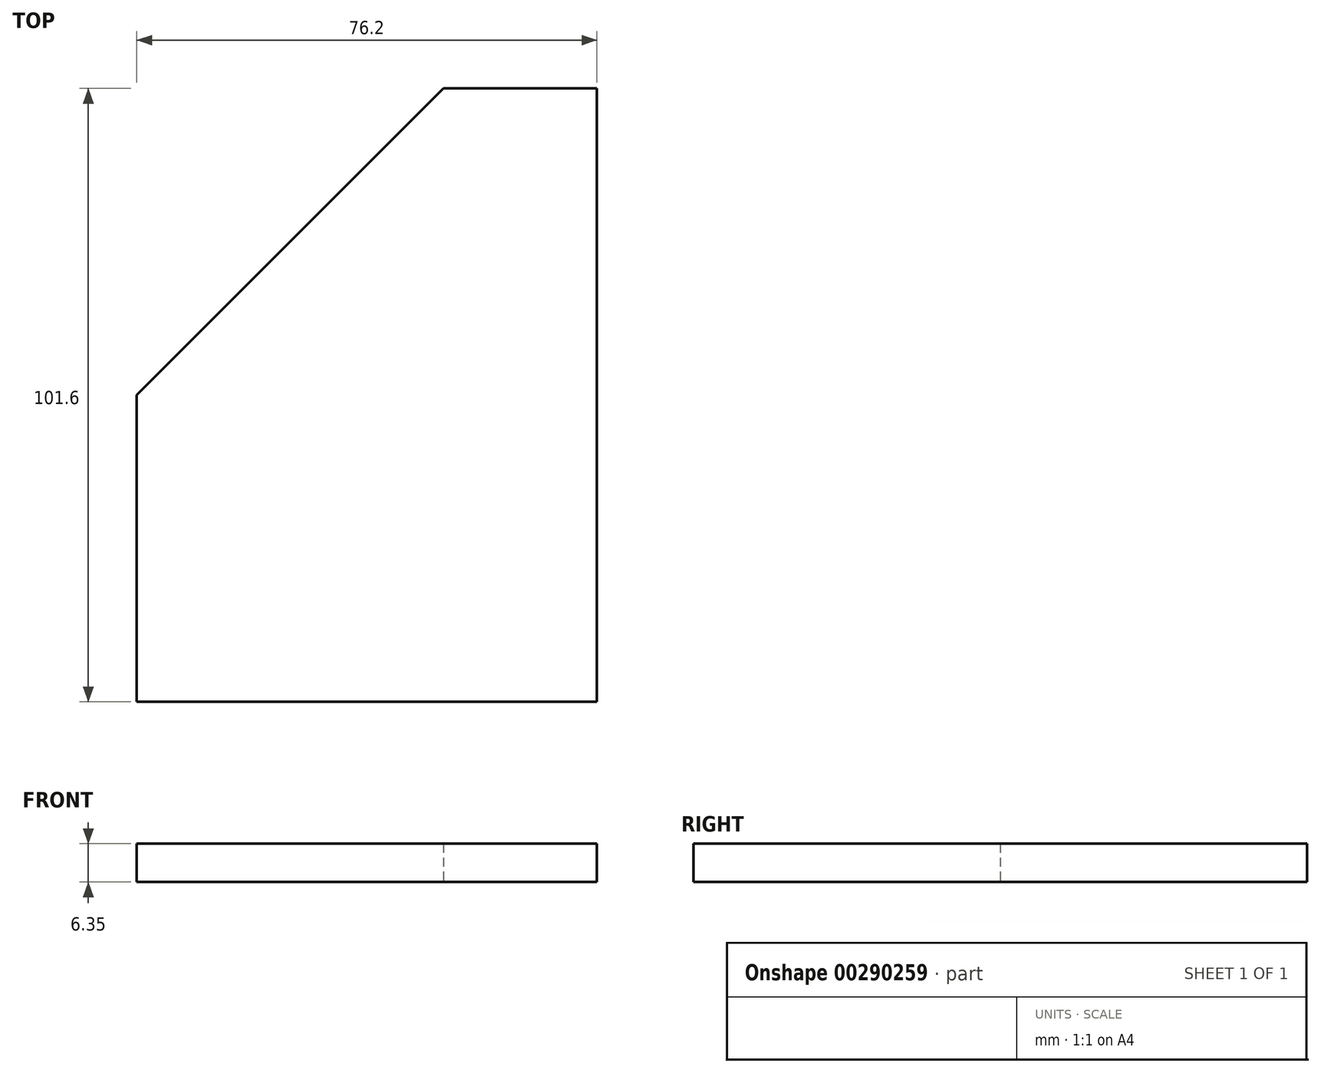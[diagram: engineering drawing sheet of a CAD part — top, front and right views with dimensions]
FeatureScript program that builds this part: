
annotation { "Feature Type Name" : "Feature", "Feature Type Description" : "" }
export const myFeature = defineFeature(function(context is Context, id is Id, definition is map)
    precondition{}
    {
        {
            var Q0;
            Q0=qCreatedBy(makeId("Top.planeOp"),FACE);
            var sketch = newSketch(context, id + "F0", { "sketchPlane" : qUnion([Q0])});
            skLineSegment(sketch, "E0.top", {"start": v(0, -101.6) * mm, "end": v(76.2, -101.6) * mm});
            skLineSegment(sketch, "E0.left", {"start": v(0, -50.8) * mm, "end": v(0, -101.6) * mm});
            skLineSegment(sketch, "E0.right", {"start": v(76.2, 0) * mm, "end": v(76.2, -101.6) * mm});
            skLineSegment(sketch, "E1", {"start": v(50.8, 0) * mm, "end": v(0, -50.8) * mm});
            skLineSegment(sketch, "E2", {"start": v(50.8, 0) * mm, "end": v(76.2, 0) * mm});
            skSolve(sketch);
        }
        {
            var Q0;
            Q0=makeQuery(id+"F0.imprint","IMPRINT",FACE,{"disambiguationData":[TD([[makeQuery(id+"F0.imprint","IMPRINT",EDGE,{"derivedFrom":sQuery(id+"F0.wireOp",EDGE,"E0.top")}),1.0]])]});
            extrude(context, id + "F1", {"entities" : qUnion([Q0]), "depth" : 6.35 * mm});
        }
    });
